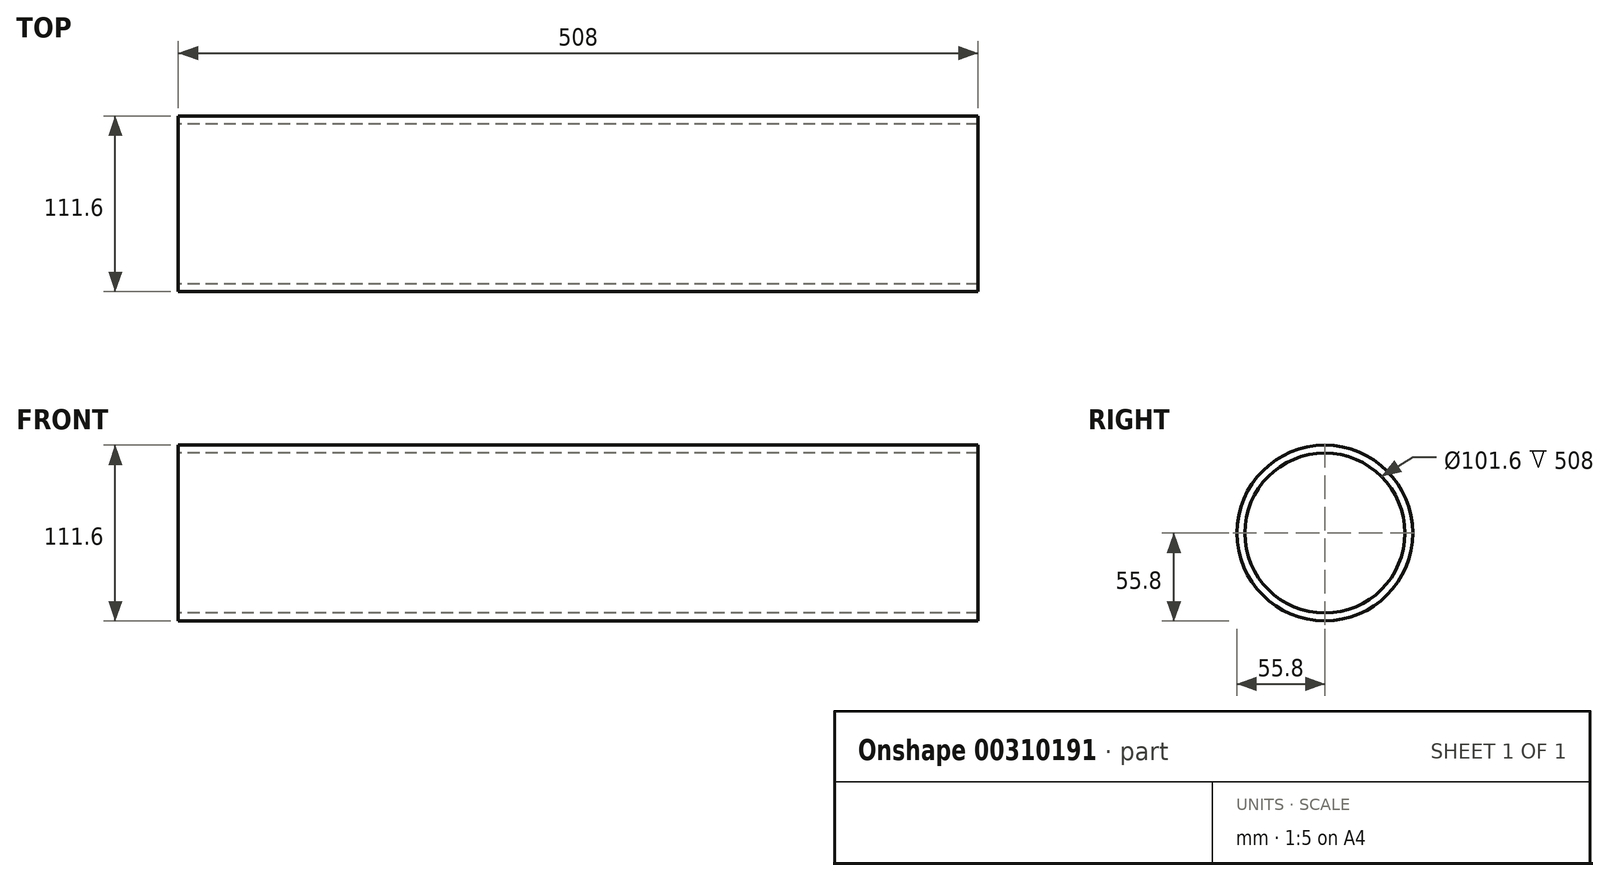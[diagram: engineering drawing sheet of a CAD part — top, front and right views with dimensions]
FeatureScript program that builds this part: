
annotation { "Feature Type Name" : "Feature", "Feature Type Description" : "" }
export const myFeature = defineFeature(function(context is Context, id is Id, definition is map)
    precondition{}
    {
        {
            var Q0;
            Q0=qCreatedBy(makeId("Right.planeOp"),FACE);
            var sketch = newSketch(context, id + "F0", { "sketchPlane" : qUnion([Q0])});
            skCircle(sketch, "E0", {"center": v(0, 0) * mm, "radius": 50.8 * mm});
            skCircle(sketch, "E1", {"center": v(0, 0) * mm, "radius": 55.8 * mm});
            skSolve(sketch);
        }
        {
            var Q0;
            Q0 = qSketchRegion(id + "F0", true);
            extrude(context, id + "F1", {"entities" : qUnion([Q0]), "endBound" : BoundingType.SYMMETRIC, "depth" : (20 * 25.4) * mm});
        }
    });
